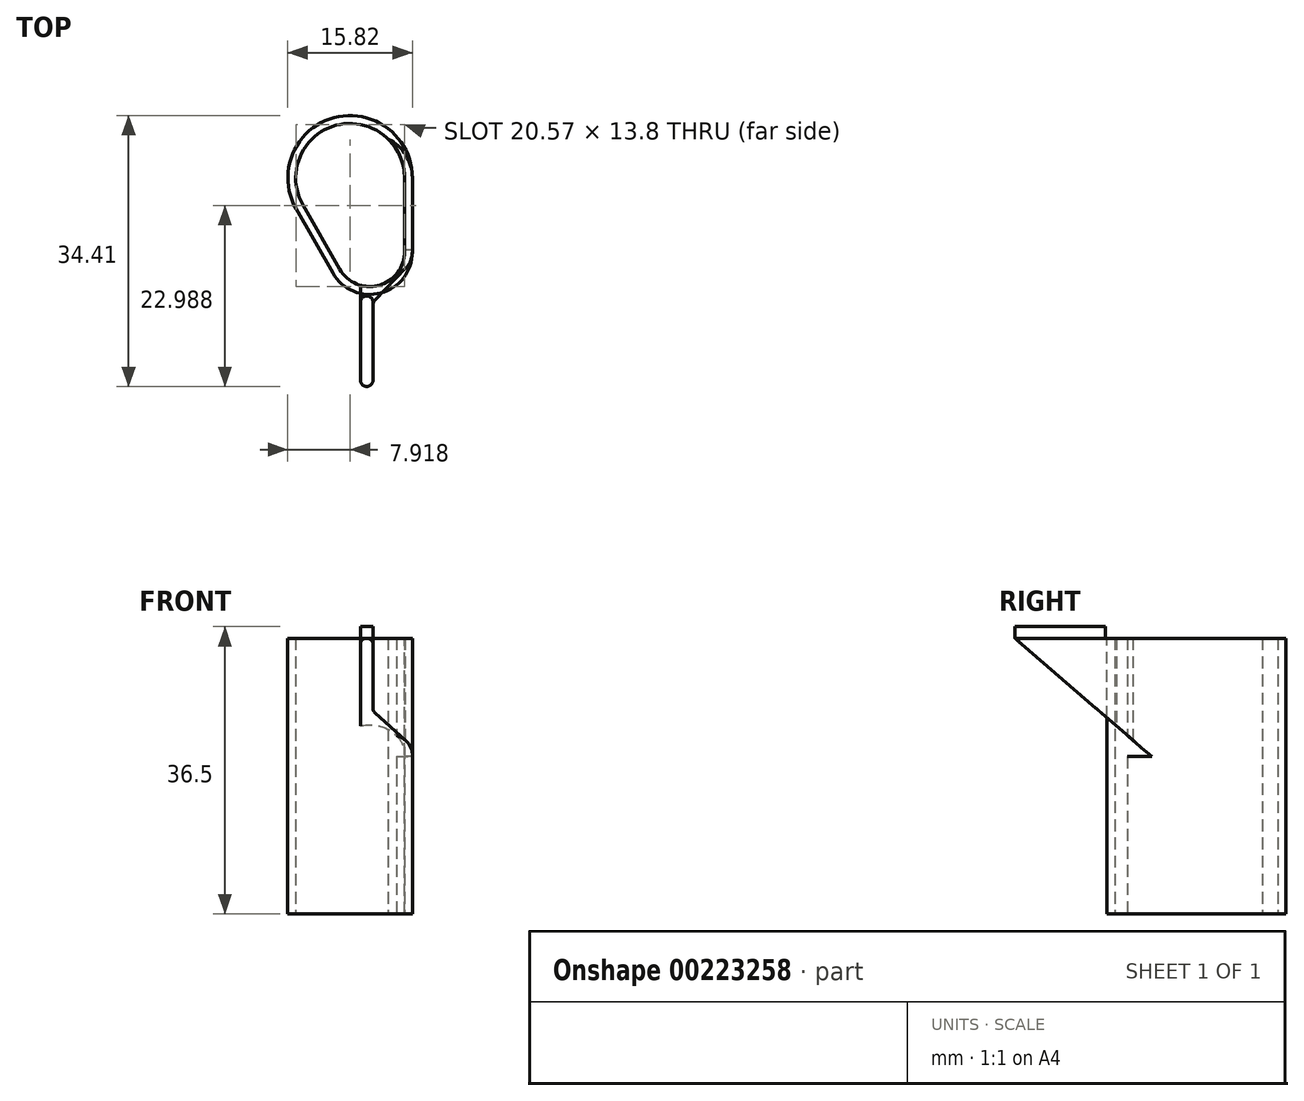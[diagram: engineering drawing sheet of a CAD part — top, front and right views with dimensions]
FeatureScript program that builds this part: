
annotation { "Feature Type Name" : "Feature", "Feature Type Description" : "" }
export const myFeature = defineFeature(function(context is Context, id is Id, definition is map)
    precondition{}
    {
        {
            var Q0;
            Q0=qCreatedBy(makeId("Top.planeOp"),FACE);
            var sketch = newSketch(context, id + "F0", { "sketchPlane" : qUnion([Q0])});
            skCircle(sketch, "E0", {"center": v(0, 0) * mm, "radius": 4.5 * mm});
            skCircle(sketch, "E1", {"center": v(0, 0) * mm, "radius": 5.5 * mm});
            skLineSegment(sketch, "E2", {"start": v(0.5, -15.8) * mm, "end": v(0.5, -25.7) * mm});
            skArc(sketch, "E3", {"start": v(-1.1, -25.7) * mm, "mid": v(-0.3, -26.5) * mm, "end": v(0.5, -25.7) * mm});
            skArc(sketch, "E4", {"start": v(0.5, -15.8) * mm, "mid": v(-0.3, -15) * mm, "end": v(-1.1, -15.8) * mm});
            skLineSegment(sketch, "E5", {"start": v(-1.1, -15.8) * mm, "end": v(-1.1, -25.7) * mm});
            skLineSegment(sketch, "E6", {"start": v(-0.3, -26.5) * mm, "end": v(-10.58, -26.5) * mm, "construction": true});
            skLineSegment(sketch, "E7", {"start": v(-0.3, -15) * mm, "end": v(-9.06, -15) * mm, "construction": true});
            skLineSegment(sketch, "E8", {"start": v(-4.5, 0) * mm, "end": v(-4.5, 7.42) * mm, "construction": true});
            skLineSegment(sketch, "E9", {"start": v(0, 4.5) * mm, "end": v(18.91, 4.5) * mm, "construction": true});
            skSolve(sketch);
        }
        {
            var Q0;
            Q0=qSketchRegion(id+"F0",true);
            extrude(context, id + "F1", {"entities" : qUnion([Q0]), "depth" : 35 * mm});
        }
        {
            var Q0;
            Q0=makeQuery(id+"F1.opExtrude","CAP_FACE",FACE,{"disambiguationData":[OSD([sQuery(id+"F0.wireOp",EDGE,"E2"),sQuery(id+"F0.wireOp",EDGE,"E3"),sQuery(id+"F0.wireOp",EDGE,"E4"),sQuery(id+"F0.wireOp",EDGE,"E5")])],"isStart":false});
            var sketch = newSketch(context, id + "F2", { "sketchPlane" : qUnion([Q0])});
            skArc(sketch, "E10.0.0", {"start": v(0.5, -15.8) * mm, "mid": v(-0.3, -15) * mm, "end": v(-1.1, -15.8) * mm});
            skLineSegment(sketch, "E10.0.1", {"start": v(-1.1, -15.8) * mm, "end": v(-1.1, -25.7) * mm});
            skArc(sketch, "E10.0.2", {"start": v(-1.1, -25.7) * mm, "mid": v(-0.3, -26.5) * mm, "end": v(0.5, -25.7) * mm});
            skLineSegment(sketch, "E10.0.3", {"start": v(0.5, -25.7) * mm, "end": v(0.5, -15.8) * mm});
            skSolve(sketch);
        }
        {
            var Q0;
            Q0=makeQuery(id+"F2.imprint","IMPRINT",FACE,{"disambiguationData":[TD([[makeQuery(id+"F2.imprint","IMPRINT",EDGE,{"derivedFrom":sQuery(id+"F2.wireOp",EDGE,"E10.0.0")}),1.0]])]});
            extrude(context, id + "F3", {"entities" : qUnion([Q0]), "operationType" : NewBodyOperationType.ADD, "depth" : 1.5 * mm});
        }
        {
            var Q0;
            Q0=makeQuery(id+"F1.opExtrude","CAP_FACE",FACE,{"disambiguationData":[OSD([sQuery(id+"F0.wireOp",EDGE,"E2"),sQuery(id+"F0.wireOp",EDGE,"E3"),sQuery(id+"F0.wireOp",EDGE,"E4"),sQuery(id+"F0.wireOp",EDGE,"E5")])],"isStart":true});
            var sketch = newSketch(context, id + "F4", { "sketchPlane" : qUnion([Q0])});
            skArc(sketch, "E11.0.0", {"start": v(-1.1, 15.8) * mm, "mid": v(-0.3, 15) * mm, "end": v(0.5, 15.8) * mm});
            skLineSegment(sketch, "E11.0.1", {"start": v(0.5, 15.8) * mm, "end": v(0.5, 25.7) * mm});
            skArc(sketch, "E11.0.2", {"start": v(0.5, 25.7) * mm, "mid": v(-0.3, 26.5) * mm, "end": v(-1.1, 25.7) * mm});
            skLineSegment(sketch, "E11.0.3", {"start": v(-1.1, 25.7) * mm, "end": v(-1.1, 15.8) * mm});
            skSolve(sketch);
        }
        {
            var Q0;
            Q0=makeQuery(id+"F4.imprint","IMPRINT",FACE,{"disambiguationData":[TD([[makeQuery(id+"F4.imprint","IMPRINT",EDGE,{"derivedFrom":sQuery(id+"F4.wireOp",EDGE,"E11.0.0")}),-1.0]])]});
            extrude(context, id + "F5", {"entities" : qUnion([Q0]), "operationType" : NewBodyOperationType.REMOVE, "oppositeDirection" : true, "depth" : 35 * mm});
        }
        {
            var Q0;
            Q0=makeQuery(id+"F1.opExtrude","CAP_FACE",FACE,{"disambiguationData":[OSD([sQuery(id+"F0.wireOp",EDGE,"E0"),sQuery(id+"F0.wireOp",EDGE,"E1")])],"isStart":false});
            var sketch = newSketch(context, id + "F6", { "sketchPlane" : qUnion([Q0])});
            skLineSegment(sketch, "E12.0.0", {"start": v(0.5, -25.7) * mm, "end": v(0.5, -15.8) * mm});
            skArc(sketch, "E12.0.1", {"start": v(0.5, -15.8) * mm, "mid": v(-0.3, -15) * mm, "end": v(-1.1, -15.8) * mm});
            skLineSegment(sketch, "E12.0.2", {"start": v(-1.1, -15.8) * mm, "end": v(-1.1, -25.7) * mm});
            skArc(sketch, "E12.0.3", {"start": v(-1.1, -25.7) * mm, "mid": v(-0.3, -26.5) * mm, "end": v(0.5, -25.7) * mm});
            skLineSegment(sketch, "E13", {"start": v(-0.3, -15) * mm, "end": v(-4.82, -15) * mm});
            skLineSegment(sketch, "E14", {"start": v(0.5, 0.6) * mm, "end": v(0.5, -9.4) * mm});
            skLineSegment(sketch, "E15.0", {"start": v(4.5, 0.6) * mm, "end": v(4.5, -9.4) * mm});
            skArc(sketch, "E16", {"start": v(4.5, 0.6) * mm, "mid": v(2.5, 2.6) * mm, "end": v(0.5, 0.6) * mm});
            skArc(sketch, "E17", {"start": v(0.5, -9.4) * mm, "mid": v(2.5, -11.4) * mm, "end": v(4.5, -9.4) * mm});
            skLineSegment(sketch, "E18.0", {"start": v(5.5, 0.6) * mm, "end": v(5.5, -9.4) * mm});
            skArc(sketch, "E18.1", {"start": v(5.5, 0.6) * mm, "mid": v(2.5, 3.6) * mm, "end": v(-0.5, 0.6) * mm});
            skLineSegment(sketch, "E18.2", {"start": v(-0.5, 0.6) * mm, "end": v(-0.5, -9.4) * mm});
            skArc(sketch, "E18.3", {"start": v(-0.5, -9.4) * mm, "mid": v(2.5, -12.4) * mm, "end": v(5.5, -9.4) * mm});
            skLineSegment(sketch, "E19", {"start": v(-0.1, -10.9) * mm, "end": v(-4.77, -2.73) * mm});
            skLineSegment(sketch, "E20", {"start": v(-3.9, -2.24) * mm, "end": v(0.76, -10.4) * mm});
            skSolve(sketch);
        }
        {
            var Q0;
            {var subQ5=sQuery(id+"F6.wireOp",EDGE,"E19");Q0=makeQuery(id+"F6.imprint","IMPRINT",FACE,{"disambiguationData":[TD([[makeQuery(id+"F6.imprint","IMPRINT",EDGE,{"derivedFrom":subQ5}),-1.0]])]});}
            var Q1;
            {var subQ9=sQuery(id+"F6.wireOp",EDGE,"E17");var subQ10=sQuery(id+"F6.wireOp",EDGE,"E15.0");var subQ11=makeQuery(id+"F6.imprint","INTERSECT",VERTEX,{"derivedFrom":[subQ10,subQ9]});Q1=makeQuery(id+"F6.imprint","IMPRINT",FACE,{"disambiguationData":[TD([[makeQuery(id+"F6.imprint","IMPRINT",EDGE,{"disambiguationData":[TD([[subQ11,1.0]])],"derivedFrom":subQ10}),1.0]])]});}
            extrude(context, id + "F7", {"entities" : qUnion([Q0, Q1]), "operationType" : NewBodyOperationType.ADD, "oppositeDirection" : true, "depth" : 35 * mm});
        }
        {
            var Q0;
            {var subQ0=sQuery(id+"F0.wireOp",EDGE,"E1");Q0=makeQuery(id+"F7.boolean.opBoolean","MERGE",FACE,{"derivedFrom":[makeQuery(id+"F1.opExtrude","CAP_FACE",FACE,{"disambiguationData":[OSD([sQuery(id+"F0.wireOp",EDGE,"E0"),subQ0])],"isStart":false}),makeQuery(id+"F7.opExtrude","CAP_FACE",FACE,{"disambiguationData":[OSD([subQ0,sQuery(id+"F6.wireOp",EDGE,"E15.0"),sQuery(id+"F6.wireOp",EDGE,"E17"),sQuery(id+"F6.wireOp",EDGE,"E18.0"),sQuery(id+"F6.wireOp",EDGE,"E18.3"),sQuery(id+"F6.wireOp",EDGE,"E19"),sQuery(id+"F6.wireOp",EDGE,"E20")])],"isStart":true})]});}
            var sketch = newSketch(context, id + "F8", { "sketchPlane" : qUnion([Q0])});
            skLineSegment(sketch, "E21.0.0", {"start": v(5.5, -9.4) * mm, "end": v(5.5, 0) * mm});
            skArc(sketch, "E21.0.1", {"start": v(5.5, 0) * mm, "mid": v(-1.41, 5.32) * mm, "end": v(-4.77, -2.73) * mm});
            skLineSegment(sketch, "E21.0.2", {"start": v(-4.77, -2.73) * mm, "end": v(-0.1, -10.9) * mm});
            skArc(sketch, "E21.0.3", {"start": v(-0.1, -10.9) * mm, "mid": v(3.27, -12.3) * mm, "end": v(5.5, -9.4) * mm});
            skLineSegment(sketch, "E22", {"start": v(-2.33, -4.98) * mm, "end": v(-3.9, -2.24) * mm});
            skLineSegment(sketch, "E23", {"start": v(4.5, -3.16) * mm, "end": v(4.5, 0) * mm});
            skSolve(sketch);
        }
        {
            var Q0;
            {var subQ0=sQuery(id+"F8.wireOp",EDGE,"E22");Q0=makeQuery(id+"F8.imprint","IMPRINT",FACE,{"disambiguationData":[TD([[makeQuery(id+"F8.imprint","IMPRINT",EDGE,{"derivedFrom":subQ0}),-1.0]])]});}
            extrude(context, id + "F9", {"entities" : qUnion([Q0]), "operationType" : NewBodyOperationType.REMOVE, "endBound" : BoundingType.THROUGH_ALL, "oppositeDirection" : true, "depth" : 25 * mm});
        }
        {
            var Q0;
            {var subQ0=sQuery(id+"F0.wireOp",EDGE,"E1");Q0=makeQuery(id+"F7.boolean.opBoolean","MERGE",FACE,{"derivedFrom":[makeQuery(id+"F1.opExtrude","CAP_FACE",FACE,{"disambiguationData":[OSD([sQuery(id+"F0.wireOp",EDGE,"E0"),subQ0])],"isStart":false}),makeQuery(id+"F7.opExtrude","CAP_FACE",FACE,{"disambiguationData":[OSD([subQ0,sQuery(id+"F6.wireOp",EDGE,"E15.0"),sQuery(id+"F6.wireOp",EDGE,"E17"),sQuery(id+"F6.wireOp",EDGE,"E18.0"),sQuery(id+"F6.wireOp",EDGE,"E18.3"),sQuery(id+"F6.wireOp",EDGE,"E19"),sQuery(id+"F6.wireOp",EDGE,"E20")])],"isStart":true})]});}
            var sketch = newSketch(context, id + "F10", { "sketchPlane" : qUnion([Q0])});
            skLineSegment(sketch, "E24.0.0", {"start": v(0.5, -25.7) * mm, "end": v(0.5, -15.8) * mm});
            skArc(sketch, "E24.0.1", {"start": v(0.5, -15.8) * mm, "mid": v(-0.3, -15) * mm, "end": v(-1.1, -15.8) * mm});
            skLineSegment(sketch, "E24.0.2", {"start": v(-1.1, -15.8) * mm, "end": v(-1.1, -25.7) * mm});
            skArc(sketch, "E24.0.3", {"start": v(-1.1, -25.7) * mm, "mid": v(-0.3, -26.5) * mm, "end": v(0.5, -25.7) * mm});
            skLineSegment(sketch, "E25", {"start": v(-1.1, -15.8) * mm, "end": v(-1.1, -9.15) * mm});
            skLineSegment(sketch, "E26", {"start": v(0.5, -15.8) * mm, "end": v(4.66, -11.48) * mm});
            skSolve(sketch);
        }
        {
            var Q0;
            Q0=makeQuery(id+"F10.imprint","IMPRINT",FACE,{"disambiguationData":[TD([[makeQuery(id+"F10.imprint","IMPRINT",EDGE,{"derivedFrom":sQuery(id+"F10.wireOp",EDGE,"E24.0.1")}),-1.0]])]});
            var Q1;
            Q1=makeQuery(id+"F10.imprint","IMPRINT",FACE,{"disambiguationData":[TD([[makeQuery(id+"F10.imprint","IMPRINT",EDGE,{"derivedFrom":sQuery(id+"F10.wireOp",EDGE,"E24.0.0")}),1.0]])]});
            extrude(context, id + "F11", {"entities" : qUnion([Q0, Q1]), "oppositeDirection" : true, "depth" : 15 * mm});
        }
        {
            var Q0;
            Q0=makeQuery(id+"F11.opExtrude","SWEPT_FACE",FACE,{"disambiguationData":[OSD([sQuery(id+"F10.wireOp",EDGE,"E24.0.2"),sQuery(id+"F10.wireOp",EDGE,"E25")])]});
            var sketch = newSketch(context, id + "F12", { "sketchPlane" : qUnion([Q0])});
            skLineSegment(sketch, "E27.0.0", {"start": v(15.8, 36.5) * mm, "end": v(15.8, 35) * mm});
            skLineSegment(sketch, "E27.0.1", {"start": v(15.8, 35) * mm, "end": v(15, 35) * mm});
            skLineSegment(sketch, "E27.0.2", {"start": v(15.8, 35) * mm, "end": v(15.8, 36.5) * mm});
            skLineSegment(sketch, "E27.0.3", {"start": v(15.8, 36.5) * mm, "end": v(15, 36.5) * mm});
            skLineSegment(sketch, "E28.0.0", {"start": v(25.7, 36.5) * mm, "end": v(25.7, 35) * mm});
            skLineSegment(sketch, "E28.0.1", {"start": v(25.7, 35) * mm, "end": v(26.5, 35) * mm});
            skLineSegment(sketch, "E28.0.2", {"start": v(25.7, 35) * mm, "end": v(25.7, 36.5) * mm});
            skLineSegment(sketch, "E28.0.3", {"start": v(25.7, 36.5) * mm, "end": v(26.5, 36.5) * mm});
            skLineSegment(sketch, "E29", {"start": v(15, 35) * mm, "end": v(15, 20) * mm});
            skLineSegment(sketch, "E30", {"start": v(25.7, 35) * mm, "end": v(15.8, 35) * mm});
            skLineSegment(sketch, "E31.0.1", {"start": v(25.7, 35) * mm, "end": v(25.7, 20) * mm});
            skLineSegment(sketch, "E31.0.2", {"start": v(25.7, 20) * mm, "end": v(26.5, 20) * mm});
            skLineSegment(sketch, "E31.0.3", {"start": v(25.7, 20) * mm, "end": v(25.7, 35) * mm});
            skLineSegment(sketch, "E32", {"start": v(26.5, 35) * mm, "end": v(26.5, 20) * mm});
            skLineSegment(sketch, "E33", {"start": v(26.5, 35) * mm, "end": v(9.15, 20) * mm});
            skSolve(sketch);
        }
        {
            var Q0;
            {var subQ0=sQuery(id+"F12.wireOp",EDGE,"E29");var subQ4=sQuery(id+"F12.wireOp",EDGE,"E33");var subQ5=makeQuery(id+"F12.imprint","INTERSECT",VERTEX,{"derivedFrom":[subQ0,subQ4]});Q0=makeQuery(id+"F12.imprint","IMPRINT",FACE,{"disambiguationData":[TD([[makeQuery(id+"F12.imprint","IMPRINT",EDGE,{"disambiguationData":[TD([[subQ5,-1.0]])],"derivedFrom":subQ0}),-1.0]])]});}
            var Q1;
            {var subQ0=sQuery(id+"F12.wireOp",EDGE,"E29");var subQ3=sQuery(id+"F12.wireOp",EDGE,"E33");var subQ4=makeQuery(id+"F12.imprint","INTERSECT",VERTEX,{"derivedFrom":[subQ0,subQ3]});Q1=makeQuery(id+"F12.imprint","IMPRINT",FACE,{"disambiguationData":[TD([[makeQuery(id+"F12.imprint","IMPRINT",EDGE,{"disambiguationData":[TD([[subQ4,1.0]])],"derivedFrom":subQ3}),1.0]])]});}
            var Q2;
            {var subQ0=sQuery(id+"F12.wireOp",EDGE,"E31.0.2");Q2=makeQuery(id+"F12.imprint","IMPRINT",FACE,{"disambiguationData":[TD([[makeQuery(id+"F12.imprint","IMPRINT",EDGE,{"derivedFrom":subQ0}),1.0]])]});}
            extrude(context, id + "F13", {"entities" : qUnion([Q0, Q1, Q2]), "operationType" : NewBodyOperationType.REMOVE, "oppositeDirection" : true, "depth" : 25 * mm});
        }
        {
            var Q0;
            Q0=makeQuery(id+"F11.opExtrude","SWEPT_EDGE",EDGE,{"disambiguationData":[OSD([sQuery(id+"F10.wireOp",EDGE,"E24.0.0"),sQuery(id+"F10.wireOp",EDGE,"E24.0.1"),sQuery(id+"F10.wireOp",EDGE,"E26")])]});
            fillet(context, id + "F14", {"entities" : qUnion([Q0]), "radius" : 1 * mm, "tangentPropagation" : true, "allowEdgeOverflow" : false});
        }
        {
            var Q0;
            {var subQ0=sQuery(id+"F0.wireOp",EDGE,"E1");Q0=makeQuery(id+"F7.boolean.opBoolean","MERGE",FACE,{"derivedFrom":[makeQuery(id+"F1.opExtrude","CAP_FACE",FACE,{"disambiguationData":[OSD([sQuery(id+"F0.wireOp",EDGE,"E0"),subQ0])],"isStart":false}),makeQuery(id+"F7.opExtrude","CAP_FACE",FACE,{"disambiguationData":[OSD([subQ0,sQuery(id+"F6.wireOp",EDGE,"E15.0"),sQuery(id+"F6.wireOp",EDGE,"E17"),sQuery(id+"F6.wireOp",EDGE,"E18.0"),sQuery(id+"F6.wireOp",EDGE,"E18.3"),sQuery(id+"F6.wireOp",EDGE,"E19"),sQuery(id+"F6.wireOp",EDGE,"E20")])],"isStart":true})]});}
            var sketch = newSketch(context, id + "F15", { "sketchPlane" : qUnion([Q0])});
            skLineSegment(sketch, "E34.0.0", {"start": v(5.5, -9.4) * mm, "end": v(5.5, 0) * mm});
            skArc(sketch, "E34.0.1", {"start": v(5.5, 0) * mm, "mid": v(-1.41, 5.32) * mm, "end": v(-4.77, -2.73) * mm});
            skLineSegment(sketch, "E34.0.2", {"start": v(-4.77, -2.73) * mm, "end": v(-0.1, -10.9) * mm});
            skArc(sketch, "E34.0.3", {"start": v(-0.1, -10.9) * mm, "mid": v(3.27, -12.3) * mm, "end": v(5.5, -9.4) * mm});
            skLineSegment(sketch, "E35.0", {"start": v(-9.27, -3.93) * mm, "end": v(-4.6, -12.09) * mm});
            skArc(sketch, "E36", {"start": v(-4.6, -12.09) * mm, "mid": v(1.48, -14.63) * mm, "end": v(5.5, -9.4) * mm});
            skArc(sketch, "E37", {"start": v(5.5, 0) * mm, "mid": v(-4.44, 7.64) * mm, "end": v(-9.27, -3.93) * mm});
            skSolve(sketch);
        }
        {
            var Q0;
            Q0=makeQuery(id+"F15.imprint","IMPRINT",FACE,{"disambiguationData":[TD([[makeQuery(id+"F15.imprint","IMPRINT",EDGE,{"derivedFrom":sQuery(id+"F15.wireOp",EDGE,"E34.0.1")}),-1.0]])]});
            var Q1;
            Q1=makeQuery(id+"F15.imprint","IMPRINT",FACE,{"disambiguationData":[TD([[makeQuery(id+"F15.imprint","IMPRINT",EDGE,{"derivedFrom":makeQuery(id+"F7.opExtrude","CAP_EDGE",EDGE,{"disambiguationData":[OSD([sQuery(id+"F6.wireOp",EDGE,"E17")])],"isStart":true})}),1.0]])]});
            var Q2;
            Q2=makeQuery(id+"F15.imprint","IMPRINT",FACE,{"disambiguationData":[TD([[makeQuery(id+"F15.imprint","IMPRINT",EDGE,{"derivedFrom":sQuery(id+"F15.wireOp",EDGE,"E34.0.0")}),-1.0]])]});
            extrude(context, id + "F16", {"entities" : qUnion([Q0, Q1, Q2]), "oppositeDirection" : true, "depth" : 35 * mm});
        }
        {
            var Q0;
            Q0=makeQuery(id+"F16.opExtrude","CAP_FACE",FACE,{"disambiguationData":[OSD([sQuery(id+"F15.wireOp",EDGE,"E34.0.0"),sQuery(id+"F15.wireOp",EDGE,"E35.0"),sQuery(id+"F15.wireOp",EDGE,"E36"),sQuery(id+"F15.wireOp",EDGE,"E37")])],"isStart":true});
            var sketch = newSketch(context, id + "F17", { "sketchPlane" : qUnion([Q0])});
            skArc(sketch, "E38.0.0", {"start": v(-4.6, -12.09) * mm, "mid": v(1.48, -14.63) * mm, "end": v(5.5, -9.4) * mm});
            skLineSegment(sketch, "E38.0.1", {"start": v(5.5, -9.4) * mm, "end": v(5.5, 0) * mm});
            skArc(sketch, "E38.0.2", {"start": v(5.5, 0) * mm, "mid": v(-4.44, 7.64) * mm, "end": v(-9.27, -3.93) * mm});
            skLineSegment(sketch, "E38.0.3", {"start": v(-9.27, -3.93) * mm, "end": v(-4.6, -12.09) * mm});
            skArc(sketch, "E39.0", {"start": v(-2.87, -11.1) * mm, "mid": v(0.97, -12.7) * mm, "end": v(3.5, -9.4) * mm});
            skLineSegment(sketch, "E39.1", {"start": v(-7.54, -2.94) * mm, "end": v(-2.87, -11.1) * mm});
            skArc(sketch, "E39.2", {"start": v(3.5, 0) * mm, "mid": v(-3.93, 5.71) * mm, "end": v(-7.54, -2.94) * mm});
            skLineSegment(sketch, "E39.3", {"start": v(3.5, -9.4) * mm, "end": v(3.5, 0) * mm});
            skSolve(sketch);
        }
        {
            var Q0;
            Q0=makeQuery(id+"F16.opExtrude","CAP_FACE",FACE,{"disambiguationData":[OSD([sQuery(id+"F15.wireOp",EDGE,"E34.0.0"),sQuery(id+"F15.wireOp",EDGE,"E35.0"),sQuery(id+"F15.wireOp",EDGE,"E36"),sQuery(id+"F15.wireOp",EDGE,"E37")])],"isStart":false});
            var sketch = newSketch(context, id + "F18", { "sketchPlane" : qUnion([Q0])});
            skArc(sketch, "E40.0", {"start": v(4.5, 9.4) * mm, "mid": v(1.22, 13.66) * mm, "end": v(-3.74, 11.6) * mm});
            skLineSegment(sketch, "E40.1", {"start": v(4.5, 0) * mm, "end": v(4.5, 9.4) * mm});
            skArc(sketch, "E40.2", {"start": v(-8.4, 3.43) * mm, "mid": v(-4.18, -6.68) * mm, "end": v(4.5, 0) * mm});
            skLineSegment(sketch, "E40.3", {"start": v(-3.74, 11.6) * mm, "end": v(-8.4, 3.43) * mm});
            skSolve(sketch);
        }
        {
            var Q0;
            Q0=makeQuery(id+"F18.imprint","IMPRINT",FACE,{"disambiguationData":[TD([[makeQuery(id+"F18.imprint","IMPRINT",EDGE,{"derivedFrom":sQuery(id+"F18.wireOp",EDGE,"E40.0")}),1.0]])]});
            extrude(context, id + "F19", {"entities" : qUnion([Q0]), "operationType" : NewBodyOperationType.REMOVE, "endBound" : BoundingType.THROUGH_ALL, "oppositeDirection" : true, "depth" : 25 * mm});
        }
        {
            var Q0;
            Q0=makeQuery(id+"F17.imprint","IMPRINT",FACE,{"disambiguationData":[TD([[makeQuery(id+"F17.imprint","IMPRINT",EDGE,{"derivedFrom":sQuery(id+"F17.wireOp",EDGE,"E39.0")}),1.0]])]});
            var Q1;
            Q1=makeQuery(id+"F16.opExtrude","CAP_FACE",FACE,{"disambiguationData":[OSD([sQuery(id+"F15.wireOp",EDGE,"E34.0.0"),sQuery(id+"F15.wireOp",EDGE,"E35.0"),sQuery(id+"F15.wireOp",EDGE,"E36"),sQuery(id+"F15.wireOp",EDGE,"E37")])],"isStart":false});
            extrude(context, id + "F20", {"entities" : qUnion([Q0]), "operationType" : NewBodyOperationType.REMOVE, "endBound" : BoundingType.THROUGH_ALL, "oppositeDirection" : true, "endBoundEntityFace" : qUnion([Q1]), "depth" : 25 * mm});
        }
        {
            var Q0;
            Q0=makeQuery(id+"F11.opExtrude","CAP_FACE",FACE,{"disambiguationData":[OSD([sQuery(id+"F6.wireOp",EDGE,"E18.3"),sQuery(id+"F6.wireOp",EDGE,"E19"),sQuery(id+"F10.wireOp",EDGE,"E24.0.0"),sQuery(id+"F10.wireOp",EDGE,"E24.0.2"),sQuery(id+"F10.wireOp",EDGE,"E24.0.3"),sQuery(id+"F10.wireOp",EDGE,"E25"),sQuery(id+"F10.wireOp",EDGE,"E26")])],"isStart":true});
            var sketch = newSketch(context, id + "F21", { "sketchPlane" : qUnion([Q0])});
            skLineSegment(sketch, "E41.0.0", {"start": v(-1.1, -9.15) * mm, "end": v(-1.1, -25.7) * mm});
            skArc(sketch, "E41.0.1", {"start": v(-1.1, -25.7) * mm, "mid": v(-0.87, -26.27) * mm, "end": v(-0.3, -26.5) * mm});
            skArc(sketch, "E41.0.2", {"start": v(-0.3, -26.5) * mm, "mid": v(0.27, -26.27) * mm, "end": v(0.5, -25.7) * mm});
            skLineSegment(sketch, "E41.0.3", {"start": v(0.5, -25.7) * mm, "end": v(0.5, -16.2) * mm});
            skArc(sketch, "E41.0.4", {"start": v(0.5, -16.2) * mm, "mid": v(0.57, -15.83) * mm, "end": v(0.78, -15.5) * mm});
            skLineSegment(sketch, "E41.0.5", {"start": v(0.78, -15.5) * mm, "end": v(4.66, -11.48) * mm});
            skArc(sketch, "E41.0.6", {"start": v(4.66, -11.48) * mm, "mid": v(2.13, -12.38) * mm, "end": v(-0.1, -10.9) * mm});
            skLineSegment(sketch, "E41.0.7", {"start": v(-0.1, -10.9) * mm, "end": v(-1.1, -9.15) * mm});
            skArc(sketch, "E42.0", {"start": v(-3.74, -11.6) * mm, "mid": v(1.22, -13.66) * mm, "end": v(4.5, -9.4) * mm});
            skSolve(sketch);
        }
        {
            var Q0;
            {var subQ0=sQuery(id+"F21.wireOp",EDGE,"E41.0.7");Q0=makeQuery(id+"F21.imprint","IMPRINT",FACE,{"disambiguationData":[TD([[makeQuery(id+"F21.imprint","IMPRINT",EDGE,{"derivedFrom":subQ0}),1.0]])]});}
            extrude(context, id + "F22", {"entities" : qUnion([Q0]), "operationType" : NewBodyOperationType.REMOVE, "endBound" : BoundingType.THROUGH_ALL, "oppositeDirection" : true, "depth" : 25 * mm});
        }
    });
